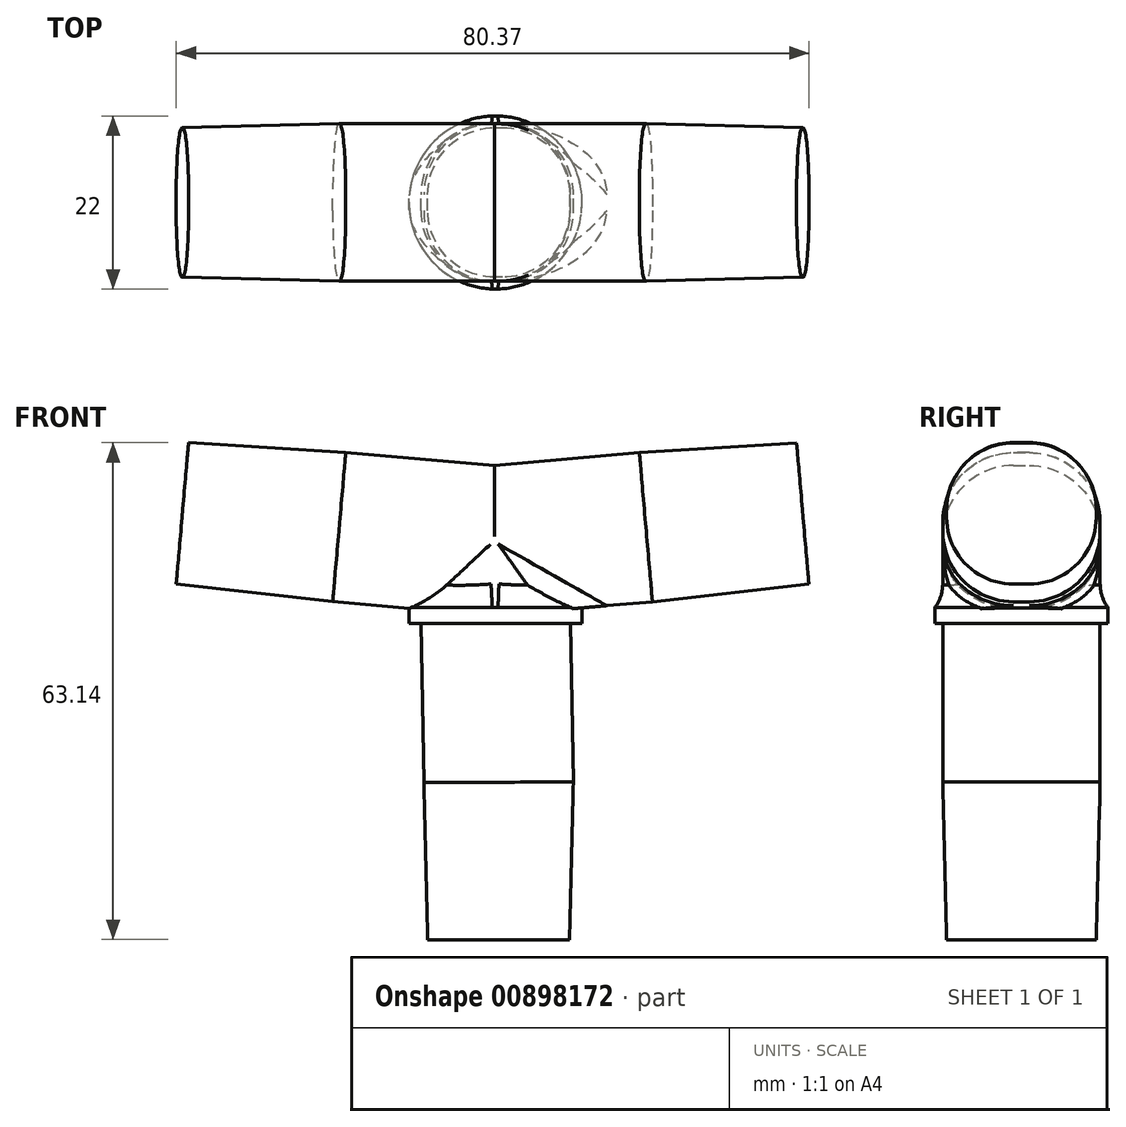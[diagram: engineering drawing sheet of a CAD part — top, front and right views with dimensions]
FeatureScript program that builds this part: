
annotation { "Feature Type Name" : "Feature", "Feature Type Description" : "" }
export const myFeature = defineFeature(function(context is Context, id is Id, definition is map)
    precondition{}
    {
        {
            var Q0;
            Q0=qCreatedBy(makeId("Front.planeOp"),FACE);
            var sketch = newSketch(context, id + "F0", { "sketchPlane" : qUnion([Q0])});
            skLineSegment(sketch, "E0", {"start": v(9.48, 0.83) * mm, "end": v(39.85, 3.49) * mm});
            skLineSegment(sketch, "E1", {"start": v(39.85, 3.49) * mm, "end": v(38.2, 22.41) * mm});
            skLineSegment(sketch, "E2", {"start": v(-0.11, 19.06) * mm, "end": v(38.2, 22.41) * mm});
            skLineSegment(sketch, "E3.MirrorCS", {"start": v(-0.11, 19.06) * mm, "end": v(-38.95, 22.46) * mm});
            skLineSegment(sketch, "E4.MirrorCS", {"start": v(-40.61, 3.5) * mm, "end": v(-38.95, 22.46) * mm});
            skLineSegment(sketch, "E5.MirrorCS", {"start": v(-9.51, 0.77) * mm, "end": v(-40.61, 3.5) * mm});
            skLineSegment(sketch, "E6.bottom", {"start": v(10.25, -41.18) * mm, "end": v(-8.75, -41.18) * mm});
            skLineSegment(sketch, "E6.left", {"start": v(10.25, -41.18) * mm, "end": v(9.48, 0.83) * mm});
            skLineSegment(sketch, "E6.right", {"start": v(-8.75, -41.18) * mm, "end": v(-9.51, 0.77) * mm});
            skPoint(sketch, "E6.middle", {"position": v(0, 0) * mm});
            skPoint(sketch, "E7.orphan", {"position": v(8.75, 41.18) * mm});
            skPoint(sketch, "E8.orphan", {"position": v(-10.25, 41.18) * mm});
            skSolve(sketch);
        }
        {
            var Q0;
            Q0 = qSketchRegion(id + "F0", true);
            extrude(context, id + "F1", {"entities" : qUnion([Q0]), "depth" : 20 * mm, "offsetDistance" : 25 * mm, "symmetric" : true});
        }
        {
            var Q0;
            Q0=makeQuery(id+"F1.opExtrude","CAP_EDGE",EDGE,{"disambiguationData":[OSD([sQuery(id+"F0.wireOp",EDGE,"E6.left")])],"isStart":false});
            var Q1;
            Q1=makeQuery(id+"F1.opExtrude","CAP_EDGE",EDGE,{"disambiguationData":[OSD([sQuery(id+"F0.wireOp",EDGE,"E6.left")])],"isStart":true});
            var Q2;
            Q2=makeQuery(id+"F1.opExtrude","CAP_EDGE",EDGE,{"disambiguationData":[OSD([sQuery(id+"F0.wireOp",EDGE,"E6.right")])],"isStart":true});
            var Q3;
            Q3=makeQuery(id+"F1.opExtrude","CAP_EDGE",EDGE,{"disambiguationData":[OSD([sQuery(id+"F0.wireOp",EDGE,"E6.right")])],"isStart":false});
            fillet(context, id + "F2", {"entities" : qUnion([Q0, Q1, Q2, Q3]), "tangentPropagation" : true, "radius" : 9 * mm, "defaultsChanged" : true, "vertexSettings" : [], "allowEdgeOverflow" : false});
        }
        {
            var Q0;
            Q0=makeQuery(id+"F1.opExtrude","CAP_EDGE",EDGE,{"disambiguationData":[OSD([sQuery(id+"F0.wireOp",EDGE,"E5.MirrorCS")])],"isStart":true});
            var Q1;
            Q1=makeQuery(id+"F1.opExtrude","CAP_EDGE",EDGE,{"disambiguationData":[OSD([sQuery(id+"F0.wireOp",EDGE,"E3.MirrorCS")])],"isStart":true});
            var Q2;
            Q2=makeQuery(id+"F1.opExtrude","CAP_EDGE",EDGE,{"disambiguationData":[OSD([sQuery(id+"F0.wireOp",EDGE,"E2")])],"isStart":true});
            var Q3;
            Q3=makeQuery(id+"F1.opExtrude","CAP_EDGE",EDGE,{"disambiguationData":[OSD([sQuery(id+"F0.wireOp",EDGE,"E0")])],"isStart":true});
            var Q4;
            Q4=makeQuery(id+"F1.opExtrude","CAP_EDGE",EDGE,{"disambiguationData":[OSD([sQuery(id+"F0.wireOp",EDGE,"E5.MirrorCS")])],"isStart":false});
            var Q5;
            Q5=makeQuery(id+"F1.opExtrude","CAP_EDGE",EDGE,{"disambiguationData":[OSD([sQuery(id+"F0.wireOp",EDGE,"E0")])],"isStart":false});
            var Q6;
            Q6=makeQuery(id+"F1.opExtrude","CAP_EDGE",EDGE,{"disambiguationData":[OSD([sQuery(id+"F0.wireOp",EDGE,"E2")])],"isStart":false});
            var Q7;
            Q7=makeQuery(id+"F1.opExtrude","CAP_EDGE",EDGE,{"disambiguationData":[OSD([sQuery(id+"F0.wireOp",EDGE,"E3.MirrorCS")])],"isStart":false});
            fillet(context, id + "F3", {"entities" : qUnion([Q0, Q1, Q2, Q3, Q4, Q5, Q6, Q7]), "tangentPropagation" : true, "radius" : 9 * mm, "defaultsChanged" : true, "vertexSettings" : [], "allowEdgeOverflow" : false});
        }
        {
            var Q0;
            Q0=qCreatedBy(makeId("Top.planeOp"),FACE);
            var sketch = newSketch(context, id + "F4", { "sketchPlane" : qUnion([Q0])});
            skCircle(sketch, "E9", {"center": v(0, 0) * mm, "radius": 11 * mm});
            skSolve(sketch);
        }
        {
            var Q0;
            Q0 = qSketchRegion(id + "F4", true);
            extrude(context, id + "F5", {"entities" : qUnion([Q0]), "operationType" : NewBodyOperationType.ADD, "depth" : 2 * mm, "offsetDistance" : 25 * mm, "symmetric" : true});
        }
        {
            var Q0;
            {var subQ0=sQuery(id+"F0.wireOp",EDGE,"E6.left");Q0=makeQuery(id+"F3.opFillet","BLEND_EDGE",EDGE,{"blendedFrom":[makeQuery(id+"F1.opExtrude","CAP_EDGE",EDGE,{"disambiguationData":[OSD([sQuery(id+"F0.wireOp",EDGE,"E5.MirrorCS")])],"isStart":true}),makeQuery(id+"F2.opFillet","BLEND_FACE",FACE,{"disambiguationData":[OSD([subQ0]),TDD([makeQuery(id+"F1.opExtrude","CAP_EDGE",EDGE,{"disambiguationData":[OSD([subQ0])],"isStart":true})])]})],"blendedInto":[makeQuery(id+"F2.opFillet","BLEND_FACE",FACE,{"disambiguationData":[OSD([subQ0]),TDD([makeQuery(id+"F1.opExtrude","CAP_EDGE",EDGE,{"disambiguationData":[OSD([subQ0])],"isStart":true})])]})]});}
            var Q1;
            {var subQ0=sQuery(id+"F0.wireOp",EDGE,"E6.left");Q1=makeQuery(id+"F3.opFillet","BLEND_EDGE",EDGE,{"blendedFrom":[makeQuery(id+"F1.opExtrude","CAP_EDGE",EDGE,{"disambiguationData":[OSD([sQuery(id+"F0.wireOp",EDGE,"E0")])],"isStart":true}),makeQuery(id+"F2.opFillet","BLEND_FACE",FACE,{"disambiguationData":[OSD([subQ0]),TDD([makeQuery(id+"F1.opExtrude","CAP_EDGE",EDGE,{"disambiguationData":[OSD([subQ0])],"isStart":true})])]})],"blendedInto":[makeQuery(id+"F2.opFillet","BLEND_FACE",FACE,{"disambiguationData":[OSD([subQ0]),TDD([makeQuery(id+"F1.opExtrude","CAP_EDGE",EDGE,{"disambiguationData":[OSD([subQ0])],"isStart":true})])]})]});}
            var Q2;
            {var subQ0=sQuery(id+"F0.wireOp",EDGE,"E6.left");Q2=makeQuery(id+"F5.boolean.opBoolean","INTERSECT",EDGE,{"derivedFrom":[makeQuery(id+"F2.opFillet","BLEND_FACE",FACE,{"disambiguationData":[OSD([subQ0]),TDD([makeQuery(id+"F1.opExtrude","CAP_EDGE",EDGE,{"disambiguationData":[OSD([subQ0])],"isStart":true})])]}),makeQuery(id+"F5.opExtrude","CAP_FACE",FACE,{"disambiguationData":[OSD([sQuery(id+"F4.wireOp",EDGE,"E9")])],"isStart":false})]});}
            var Q3;
            {var subQ0=sQuery(id+"F0.wireOp",EDGE,"E6.left");Q3=makeQuery(id+"F3.opFillet","BLEND_EDGE",EDGE,{"blendedFrom":[makeQuery(id+"F1.opExtrude","CAP_EDGE",EDGE,{"disambiguationData":[OSD([sQuery(id+"F0.wireOp",EDGE,"E5.MirrorCS")])],"isStart":false}),makeQuery(id+"F2.opFillet","BLEND_FACE",FACE,{"disambiguationData":[OSD([subQ0]),TDD([makeQuery(id+"F1.opExtrude","CAP_EDGE",EDGE,{"disambiguationData":[OSD([subQ0])],"isStart":false})])]})],"blendedInto":[makeQuery(id+"F2.opFillet","BLEND_FACE",FACE,{"disambiguationData":[OSD([subQ0]),TDD([makeQuery(id+"F1.opExtrude","CAP_EDGE",EDGE,{"disambiguationData":[OSD([subQ0])],"isStart":false})])]})]});}
            var Q4;
            {var subQ0=sQuery(id+"F0.wireOp",EDGE,"E6.left");Q4=makeQuery(id+"F3.opFillet","BLEND_EDGE",EDGE,{"blendedFrom":[makeQuery(id+"F1.opExtrude","CAP_EDGE",EDGE,{"disambiguationData":[OSD([sQuery(id+"F0.wireOp",EDGE,"E0")])],"isStart":false}),makeQuery(id+"F2.opFillet","BLEND_FACE",FACE,{"disambiguationData":[OSD([subQ0]),TDD([makeQuery(id+"F1.opExtrude","CAP_EDGE",EDGE,{"disambiguationData":[OSD([subQ0])],"isStart":false})])]})],"blendedInto":[makeQuery(id+"F2.opFillet","BLEND_FACE",FACE,{"disambiguationData":[OSD([subQ0]),TDD([makeQuery(id+"F1.opExtrude","CAP_EDGE",EDGE,{"disambiguationData":[OSD([subQ0])],"isStart":false})])]})]});}
            var Q5;
            {var subQ0=sQuery(id+"F0.wireOp",EDGE,"E6.left");Q5=makeQuery(id+"F5.boolean.opBoolean","INTERSECT",EDGE,{"derivedFrom":[makeQuery(id+"F2.opFillet","BLEND_FACE",FACE,{"disambiguationData":[OSD([subQ0]),TDD([makeQuery(id+"F1.opExtrude","CAP_EDGE",EDGE,{"disambiguationData":[OSD([subQ0])],"isStart":false})])]}),makeQuery(id+"F5.opExtrude","CAP_FACE",FACE,{"disambiguationData":[OSD([sQuery(id+"F4.wireOp",EDGE,"E9")])],"isStart":false})]});}
            fillet(context, id + "F6", {"entities" : qUnion([Q0, Q1, Q2, Q3, Q4, Q5]), "tangentPropagation" : true, "radius" : 5 * mm, "defaultsChanged" : false, "vertexSettings" : [], "allowEdgeOverflow" : false});
        }
        {
            var Q0;
            Q0=makeQuery(id+"F3.opFillet","BLEND_EDGE",EDGE,{"blendedFrom":[makeQuery(id+"F1.opExtrude","CAP_EDGE",EDGE,{"disambiguationData":[OSD([sQuery(id+"F0.wireOp",EDGE,"E3.MirrorCS")])],"isStart":true}),makeQuery(id+"F1.opExtrude","SWEPT_FACE",FACE,{"disambiguationData":[OSD([sQuery(id+"F0.wireOp",EDGE,"E4.MirrorCS")])]})],"blendedInto":[makeQuery(id+"F1.opExtrude","SWEPT_FACE",FACE,{"disambiguationData":[OSD([sQuery(id+"F0.wireOp",EDGE,"E4.MirrorCS")])]})]});
            var Q1;
            Q1=makeQuery(id+"F3.opFillet","BLEND_EDGE",EDGE,{"blendedFrom":[makeQuery(id+"F1.opExtrude","CAP_EDGE",EDGE,{"disambiguationData":[OSD([sQuery(id+"F0.wireOp",EDGE,"E2")])],"isStart":true}),makeQuery(id+"F1.opExtrude","SWEPT_FACE",FACE,{"disambiguationData":[OSD([sQuery(id+"F0.wireOp",EDGE,"E1")])]})],"blendedInto":[makeQuery(id+"F1.opExtrude","SWEPT_FACE",FACE,{"disambiguationData":[OSD([sQuery(id+"F0.wireOp",EDGE,"E1")])]})]});
            var Q2;
            Q2=makeQuery(id+"F2.opFillet","BLEND_EDGE",EDGE,{"blendedFrom":[makeQuery(id+"F1.opExtrude","CAP_EDGE",EDGE,{"disambiguationData":[OSD([sQuery(id+"F0.wireOp",EDGE,"E6.left")])],"isStart":false}),makeQuery(id+"F1.opExtrude","SWEPT_FACE",FACE,{"disambiguationData":[OSD([sQuery(id+"F0.wireOp",EDGE,"E6.bottom")])]})],"blendedInto":[makeQuery(id+"F1.opExtrude","SWEPT_FACE",FACE,{"disambiguationData":[OSD([sQuery(id+"F0.wireOp",EDGE,"E6.bottom")])]})]});
            var Q3;
            Q3=makeQuery(id+"F2.opFillet","BLEND_EDGE",EDGE,{"blendedFrom":[makeQuery(id+"F1.opExtrude","CAP_EDGE",EDGE,{"disambiguationData":[OSD([sQuery(id+"F0.wireOp",EDGE,"E6.left")])],"isStart":true}),makeQuery(id+"F1.opExtrude","SWEPT_FACE",FACE,{"disambiguationData":[OSD([sQuery(id+"F0.wireOp",EDGE,"E6.bottom")])]})],"blendedInto":[makeQuery(id+"F1.opExtrude","SWEPT_FACE",FACE,{"disambiguationData":[OSD([sQuery(id+"F0.wireOp",EDGE,"E6.bottom")])]})]});
            chamfer(context, id + "F7", {"entities" : qUnion([Q0, Q1, Q2, Q3]), "chamferType" : ChamferType.TWO_OFFSETS, "width1" : .5 * mm, "oppositeDirection" : false, "width2" : 20 * mm, "tangentPropagation" : true});
        }
        {
            var Q0;
            Q0=qCreatedBy(makeId("Front.planeOp"),FACE);
            var sketch = newSketch(context, id + "F8", { "sketchPlane" : qUnion([Q0])});
            skLineSegment(sketch, "E10.bottom", {"start": v(11.32, 18.7) * mm, "end": v(-11.46, 18.7) * mm});
            skLineSegment(sketch, "E10.top", {"start": v(11.32, 2.15) * mm, "end": v(-11.46, 2.15) * mm});
            skLineSegment(sketch, "E10.left", {"start": v(11.32, 18.7) * mm, "end": v(11.32, 2.15) * mm});
            skLineSegment(sketch, "E10.right", {"start": v(-11.46, 18.7) * mm, "end": v(-11.46, 2.15) * mm});
            skSolve(sketch);
        }
        {
            var Q0;
            Q0 = qSketchRegion(id + "F8", true);
            extrude(context, id + "F9", {"entities" : qUnion([Q0]), "operationType" : NewBodyOperationType.ADD, "depth" : 5 * mm, "offsetDistance" : 25 * mm, "symmetric" : true});
        }
    });
